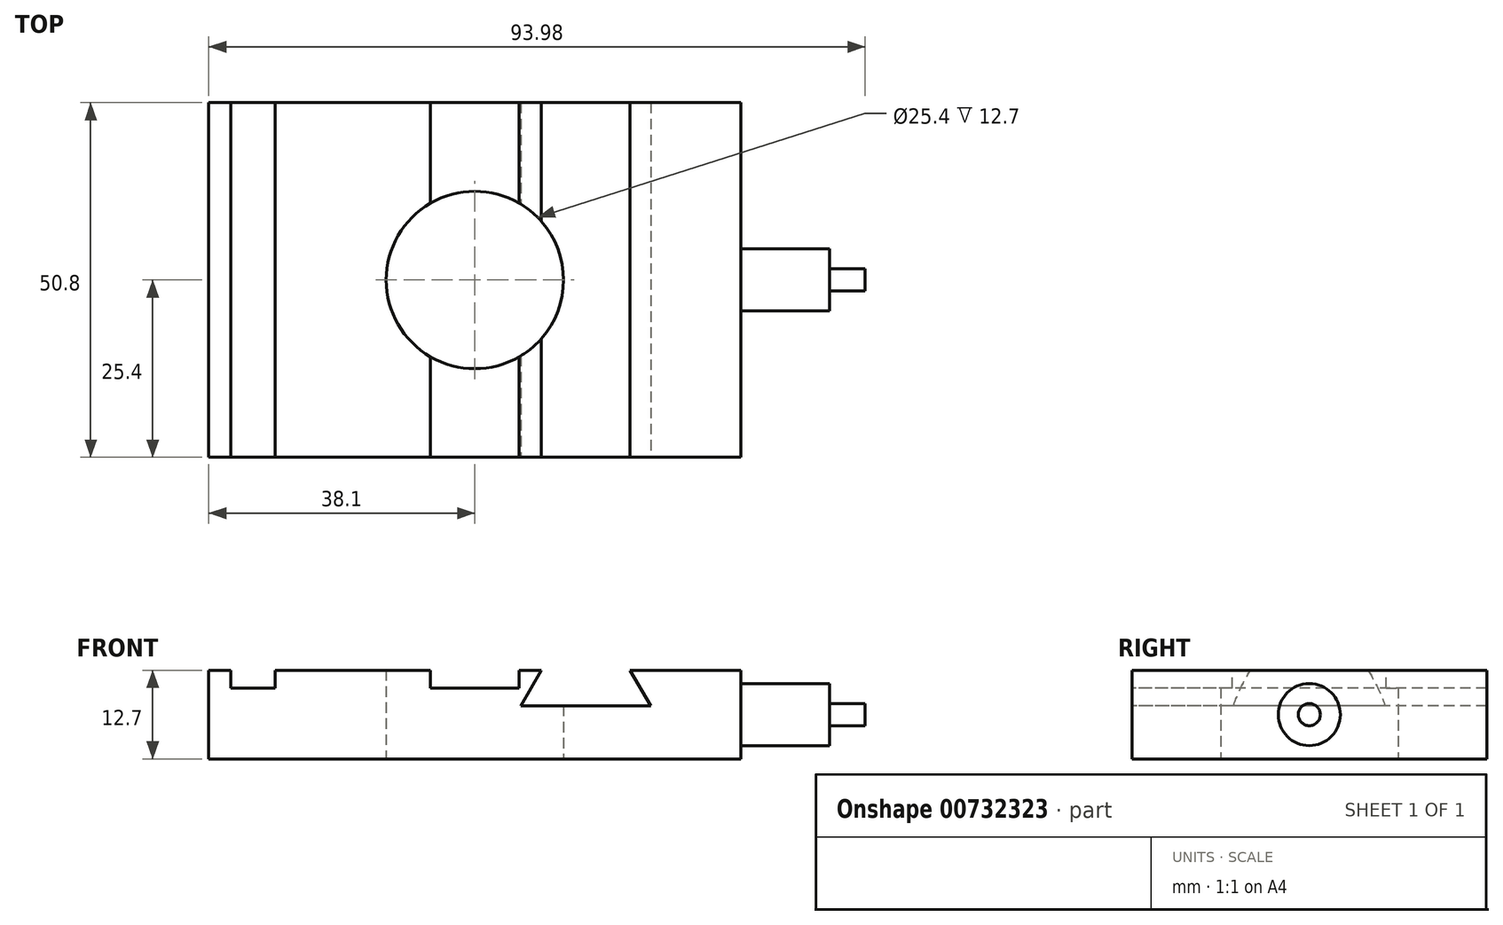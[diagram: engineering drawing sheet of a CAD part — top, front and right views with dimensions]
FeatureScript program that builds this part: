
annotation { "Feature Type Name" : "Feature", "Feature Type Description" : "" }
export const myFeature = defineFeature(function(context is Context, id is Id, definition is map)
    precondition{}
    {
        {
            var Q0;
            Q0=qCreatedBy(makeId("Top.planeOp"),FACE);
            var sketch = newSketch(context, id + "F0", { "sketchPlane" : qUnion([Q0])});
            skLineSegment(sketch, "E0.bottom", {"start": v(38.1, 25.4) * mm, "end": v(-38.1, 25.4) * mm});
            skLineSegment(sketch, "E0.top", {"start": v(38.1, -25.4) * mm, "end": v(-38.1, -25.4) * mm});
            skLineSegment(sketch, "E0.left", {"start": v(38.1, 25.4) * mm, "end": v(38.1, -25.4) * mm});
            skLineSegment(sketch, "E0.right", {"start": v(-38.1, 25.4) * mm, "end": v(-38.1, -25.4) * mm});
            skPoint(sketch, "E0.middle", {"position": v(0, 0) * mm});
            skCircle(sketch, "E1", {"center": v(0, 0) * mm, "radius": 12.7 * mm});
            skSolve(sketch);
        }
        {
            var Q0;
            Q0=makeQuery(id+"F0.imprint","IMPRINT",FACE,{"disambiguationData":[TD([[makeQuery(id+"F0.imprint","IMPRINT",EDGE,{"derivedFrom":sQuery(id+"F0.wireOp",EDGE,"E0.bottom")}),1.0]])]});
            extrude(context, id + "F1", {"entities" : qUnion([Q0]), "depth" : 12.7 * mm, "offsetDistance" : 25.4 * mm});
        }
        {
            var Q0;
            Q0=makeQuery(id+"F1.opExtrude","CAP_FACE",FACE,{"disambiguationData":[OSD([sQuery(id+"F0.wireOp",EDGE,"E0.bottom"),sQuery(id+"F0.wireOp",EDGE,"E0.top"),sQuery(id+"F0.wireOp",EDGE,"E0.left"),sQuery(id+"F0.wireOp",EDGE,"E0.right"),sQuery(id+"F0.wireOp",EDGE,"E1")])],"isStart":false});
            var sketch = newSketch(context, id + "F2", { "sketchPlane" : qUnion([Q0])});
            skLineSegment(sketch, "E2.bottom", {"start": v(-34.92, 25.4) * mm, "end": v(-28.57, 25.4) * mm});
            skLineSegment(sketch, "E2.top", {"start": v(-34.92, -25.4) * mm, "end": v(-28.57, -25.4) * mm});
            skLineSegment(sketch, "E2.left", {"start": v(-34.92, 25.4) * mm, "end": v(-34.92, -25.4) * mm});
            skLineSegment(sketch, "E2.right", {"start": v(-28.57, 25.4) * mm, "end": v(-28.57, -25.4) * mm});
            skLineSegment(sketch, "E3", {"start": v(-6.35, 25.4) * mm, "end": v(-6.35, -25.4) * mm});
            skLineSegment(sketch, "E4", {"start": v(-6.35, -25.4) * mm, "end": v(6.35, -25.4) * mm});
            skLineSegment(sketch, "E5", {"start": v(6.35, -25.4) * mm, "end": v(6.35, 25.4) * mm});
            skLineSegment(sketch, "E6", {"start": v(6.35, 25.4) * mm, "end": v(-6.35, 25.4) * mm});
            skLineSegment(sketch, "E7", {"start": v(0, 25.4) * mm, "end": v(0, -25.4) * mm, "construction": true});
            skSolve(sketch);
        }
        {
            var Q0;
            Q0=makeQuery(id+"F2.imprint","IMPRINT",FACE,{"disambiguationData":[TD([[makeQuery(id+"F2.imprint","IMPRINT",EDGE,{"derivedFrom":sQuery(id+"F2.wireOp",EDGE,"E2.bottom")}),1.0]])]});
            var Q1;
            {var subQ0=sQuery(id+"F2.wireOp",EDGE,"E4");Q1=makeQuery(id+"F2.imprint","IMPRINT",FACE,{"disambiguationData":[TD([[makeQuery(id+"F2.imprint","IMPRINT",EDGE,{"derivedFrom":subQ0}),-1.0]])]});}
            var Q2;
            {var subQ0=sQuery(id+"F2.wireOp",EDGE,"E6");Q2=makeQuery(id+"F2.imprint","IMPRINT",FACE,{"disambiguationData":[TD([[makeQuery(id+"F2.imprint","IMPRINT",EDGE,{"derivedFrom":subQ0}),1.0]])]});}
            extrude(context, id + "F3", {"entities" : qUnion([Q0, Q1, Q2]), "operationType" : NewBodyOperationType.REMOVE, "oppositeDirection" : true, "depth" : 2.54 * mm, "offsetDistance" : 25.4 * mm});
        }
        {
            var Q0;
            Q0=makeQuery(id+"F1.opExtrude","SWEPT_FACE",FACE,{"disambiguationData":[OSD([sQuery(id+"F0.wireOp",EDGE,"E0.top")])]});
            var sketch = newSketch(context, id + "F4", { "sketchPlane" : qUnion([Q0])});
            skLineSegment(sketch, "E8", {"start": v(9.53, 12.7) * mm, "end": v(6.6, 7.62) * mm});
            skLineSegment(sketch, "E9", {"start": v(6.6, 7.62) * mm, "end": v(25.16, 7.62) * mm});
            skLineSegment(sketch, "E10", {"start": v(25.16, 7.62) * mm, "end": v(22.23, 12.7) * mm});
            skLineSegment(sketch, "E11", {"start": v(22.23, 12.7) * mm, "end": v(9.53, 12.7) * mm});
            skLineSegment(sketch, "E12", {"start": v(15.88, 7.62) * mm, "end": v(15.88, 12.7) * mm, "construction": true});
            skSolve(sketch);
        }
        {
            var Q0;
            Q0=makeQuery(id+"F4.imprint","IMPRINT",FACE,{"disambiguationData":[TD([[makeQuery(id+"F4.imprint","IMPRINT",EDGE,{"derivedFrom":sQuery(id+"F4.wireOp",EDGE,"E8")}),1.0]])]});
            extrude(context, id + "F5", {"entities" : qUnion([Q0]), "operationType" : NewBodyOperationType.REMOVE, "endBound" : BoundingType.UP_TO_NEXT, "oppositeDirection" : true, "depth" : 25.4 * mm, "offsetDistance" : 25.4 * mm});
        }
        {
            var Q0;
            Q0=makeQuery(id+"F1.opExtrude","SWEPT_FACE",FACE,{"disambiguationData":[OSD([sQuery(id+"F0.wireOp",EDGE,"E0.left")])]});
            var sketch = newSketch(context, id + "F6", { "sketchPlane" : qUnion([Q0])});
            skCircle(sketch, "E13", {"center": v(0, 6.35) * mm, "radius": 4.45 * mm});
            skPoint(sketch, "E13.centerSnap0", {"position": v(-25.4, 6.35) * mm});
            skSolve(sketch);
        }
        {
            var Q0;
            Q0=makeQuery(id+"F6.imprint","IMPRINT",FACE,{"disambiguationData":[TD([[makeQuery(id+"F6.imprint","IMPRINT",EDGE,{"derivedFrom":sQuery(id+"F6.wireOp",EDGE,"E13")}),1.0]])]});
            extrude(context, id + "F7", {"entities" : qUnion([Q0]), "operationType" : NewBodyOperationType.ADD, "depth" : 12.7 * mm, "offsetDistance" : 25.4 * mm});
        }
        {
            var Q0;
            Q0=makeQuery(id+"F7.opExtrude","CAP_FACE",FACE,{"disambiguationData":[OSD([sQuery(id+"F6.wireOp",EDGE,"E13")])],"isStart":false});
            var sketch = newSketch(context, id + "F8", { "sketchPlane" : qUnion([Q0])});
            skCircle(sketch, "E14", {"center": v(0, 6.35) * mm, "radius": 1.59 * mm});
            skSolve(sketch);
        }
        {
            var Q0;
            Q0=makeQuery(id+"F8.imprint","IMPRINT",FACE,{"disambiguationData":[TD([[makeQuery(id+"F8.imprint","IMPRINT",EDGE,{"derivedFrom":sQuery(id+"F8.wireOp",EDGE,"E14")}),1.0]])]});
            extrude(context, id + "F9", {"entities" : qUnion([Q0]), "operationType" : NewBodyOperationType.ADD, "depth" : 5.08 * mm, "offsetDistance" : 25.4 * mm});
        }
    });
